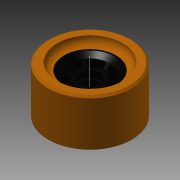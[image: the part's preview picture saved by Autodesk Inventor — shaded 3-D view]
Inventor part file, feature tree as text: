
AUTODESK INVENTOR PART (.ipt)
format: ipt  version: 2014 SP1 (Build 180222100, 222)  size: 391,680 bytes
history: native  units: in
note: dims shown in document units (in); Inventor stores cm internally (conversion verified against a paired STEP export)
features: other x3, sketch x3
ambient origin geometry x8: Origin, YZ Plane, XZ Plane, XY Plane, X Axis, Y Axis, Z Axis, Center Point
bodies: Solid1 (feature_tree)
feature tree (6):
  other  "wheel90mm.ipt"
  other  "Solid1::wheel90mm.ipt"
  other  "TaggingFeature1"
  sketch  "Sketch2"  dims[d0=0.3937in]
  sketch  "Sketch3"  dims[d2=0.38in d4=0.44in d6=0.815in d7=0.29in d9=1.025in d10=0.2898in d11=0.36in d13=1.14in d14=0.834in d15=0.0in d17=0.865in d18=0.1in d19=0.296in d20=0.0in d21=0.15in d23=0.0in d24=0.168in d25=0.18in d27=0.05in d28=2.3622in d29=360.0deg d31=0.168in d32=0.18in d34=30.0deg d35=0.09in d36=0.06in d38=0.0in d39=0.05in d40=0.02in d41=2.3622in d42=360.0deg d44=0.08in d47=0.08in d48=0.292in]
  sketch  "Sketch5"
